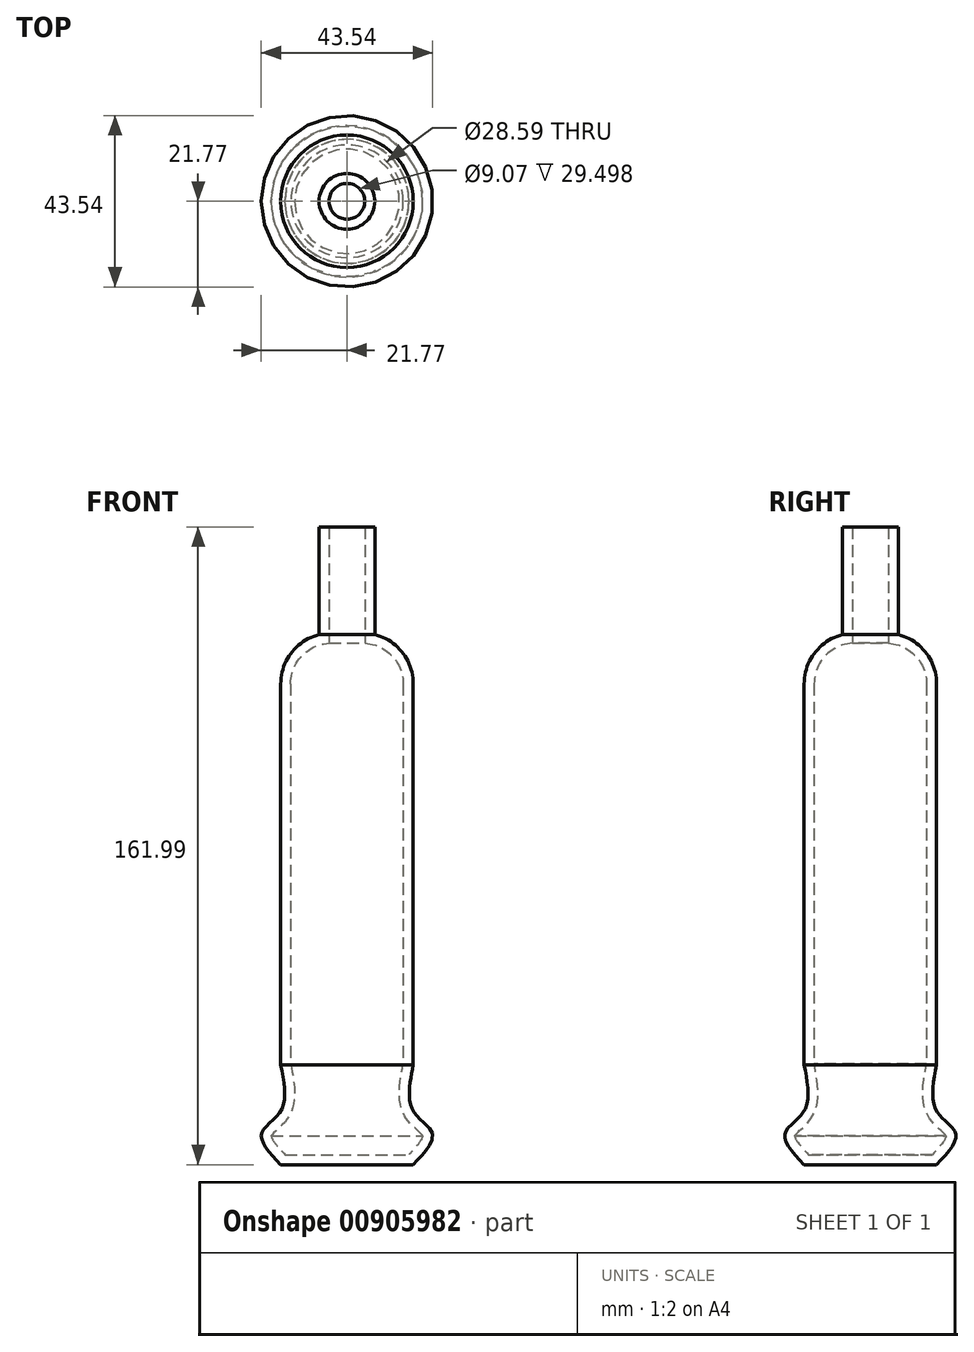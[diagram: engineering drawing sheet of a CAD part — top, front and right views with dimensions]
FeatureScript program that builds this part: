
annotation { "Feature Type Name" : "Feature", "Feature Type Description" : "" }
export const myFeature = defineFeature(function(context is Context, id is Id, definition is map)
    precondition{}
    {
        {
            var Q0;
            Q0=qCreatedBy(makeId("Front.planeOp"),FACE);
            var sketch = newSketch(context, id + "F0", { "sketchPlane" : qUnion([Q0])});
            skLineSegment(sketch, "E0", {"start": v(16.83, 49.04) * mm, "end": v(16.83, -60.26) * mm});
            skLineSegment(sketch, "E1", {"start": v(0, -85.63) * mm, "end": v(16.83, -85.63) * mm});
            skFitSpline(sketch, "E2", {"points": [v(16.83, -60.26) * mm, v(16.83, -71.97) * mm, v(21.71, -77.83) * mm, v(16.83, -85.63) * mm], "startDerivative": vector(-6.93, -35.34) * mm, "endDerivative": vector(-24.43, -25.6) * mm});
            skLineSegment(sketch, "E3", {"start": v(16.83, 49.04) * mm, "end": v(7.08, 49.04) * mm});
            skLineSegment(sketch, "E4", {"start": v(7.08, 49.04) * mm, "end": v(7.08, 76.36) * mm});
            skLineSegment(sketch, "E5", {"start": v(0, -85.63) * mm, "end": v(0, 76.36) * mm});
            skLineSegment(sketch, "E6", {"start": v(0, 76.36) * mm, "end": v(7.08, 76.36) * mm});
            skSolve(sketch);
        }
        {
            var Q0;
            Q0=makeQuery(id+"F0.imprint","IMPRINT",FACE,{"disambiguationData":[TD([[makeQuery(id+"F0.imprint","IMPRINT",EDGE,{"derivedFrom":sQuery(id+"F0.wireOp",EDGE,"E0")}),-1.0]])]});
            var Q1;
            Q1=sQuery(id+"F0.wireOp",EDGE,"E5");
            revolve(context, id + "F1", {"surfaceOperationType" : NewSurfaceOperationType.NEW, "entities" : qUnion([Q0]), "axis" : qUnion([Q1]), "revolveType" : RevolveType.FULL});
        }
        {
            var Q0;
            Q0=makeQuery(id+"F1.opRevolve","SWEPT_EDGE",EDGE,{"disambiguationData":[OSD([sQuery(id+"F0.wireOp",EDGE,"E0"),sQuery(id+"F0.wireOp",EDGE,"E3")])]});
            fillet(context, id + "F2", {"entities" : qUnion([Q0]), "radius" : 12.88 * mm, "tangentPropagation" : true, "allowEdgeOverflow" : false});
        }
        {
            var Q0;
            Q0=makeQuery(id+"F1.opRevolve","SWEPT_FACE",FACE,{"disambiguationData":[OSD([sQuery(id+"F0.wireOp",EDGE,"E6")])]});
            shell(context, id + "F3", {"entities" : qUnion([Q0]), "thickness" : 2.54 * mm});
        }
    });
